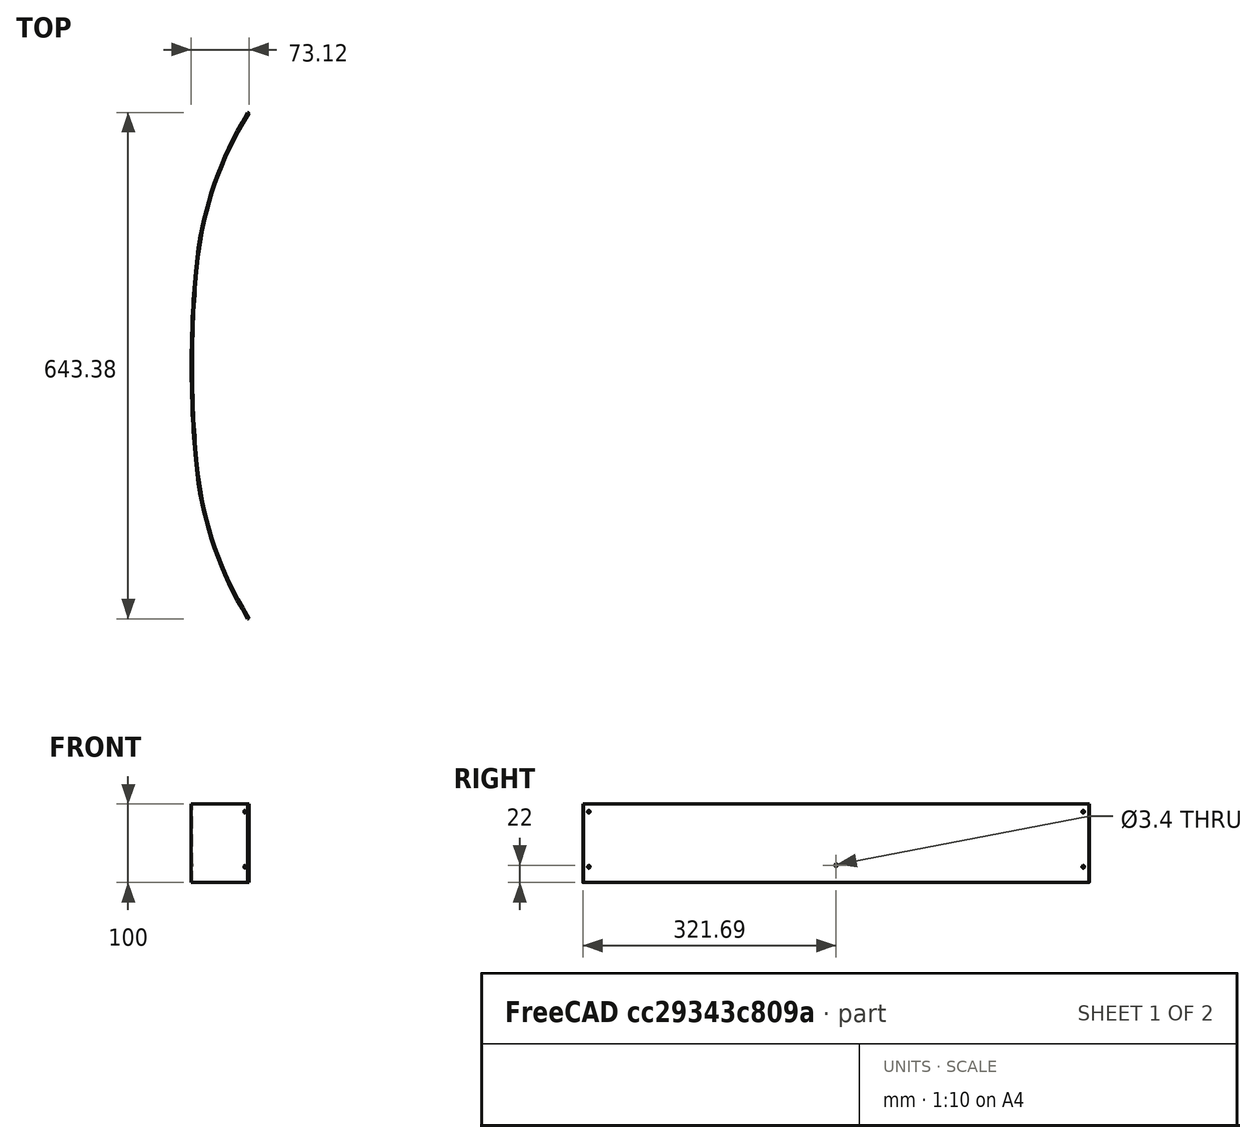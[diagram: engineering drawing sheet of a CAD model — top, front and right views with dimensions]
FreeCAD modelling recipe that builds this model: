
FCSTD DOCUMENT  (FreeCAD 1.1R38827 (Git))
Label: composit_stand3_hat_plexiglass_main
License: All rights reserved
LicenseURL: http://en.wikipedia.org/wiki/All_rights_reserved
objects: Part::Feature×1, PartDesign::SubShapeBinder×1, Part::Mirroring×1, Sketcher::SketchObject×1
note: 5 computed .brp shape members not serialized (recipe doc carries the construction recipe); baked Part::Feature solids carry a one-line shape summary decoded from their .brp
EXTERNAL_REF file=composit_stand3_hat_bottom_main.FCStd obj=Sketch001

FEATURE [Part::Feature] Body172  label="hat3_plexiglass001"
  Placement = pos=(0,0,0) rot=(0,0,1;-0.523599rad)
  shape: bbox 73.12 x 643.4 x 100 mm, 43 faces (baked)
FEATURE [PartDesign::SubShapeBinder] Binder
  BindCopyOnChange = 0
  BindMode = 0
  ClaimChildren = false
  Fuse = false
  MakeFace = true
  OffsetFill = false
  OffsetIntersection = false
  OffsetJoinType = 0
  OffsetOpenResult = false
  PartialLoad = false
  Placement = pos=(0,0,0) rot=(0,0,1;-1.0472rad)
  Relative = true
  Support = -> [<external composit_stand3_hat_bottom_main.FCStd>#Sketch001]
  _Version = 2
FEATURE [Part::Mirroring] Part__Mirroring  label="Binder (Mirror #1)"
  Base = (0,0,0)
  Normal = (0,1,0)
  Source = -> Binder
FEATURE [Sketcher::SketchObject] Sketch  label="main_sketch"
  ArcFitTolerance = 1e-06
  ExternalGeometry = -> [Body172,Part__Mirroring]
  FullyConstrained = true
  MakeInternals = false
  sketch-geometry (4):
    g0: LineSegment StartX=204.116 StartY=320.94 StartZ=0 EndX=116.713 EndY=169.553 EndZ=0
    g1: LineSegment StartX=116.713 StartY=169.553 StartZ=0 EndX=116.713 EndY=-169.553 EndZ=0
    g2: LineSegment StartX=116.713 StartY=-169.553 StartZ=0 EndX=204.116 EndY=-320.94 EndZ=0
    g3: ArcOfCircle [constr] CenterX=713.119 CenterY=9.74631 CenterZ=0 NormalX=0 NormalY=0 NormalZ=1 AngleXU=0 Radius=596.406 StartAngle=2.61799 EndAngle=3.14159
  constraints (11):
    c: Coincident(g0,g1)
    c: Coincident(g2,g1)
    c: Symmetric(g2,g0,g-1)
    c: Symmetric(g1,g0,g-1)
    c: Coincident(g0,g-3)
    c: Angle(g0) = -2.0944
    c: Coincident(g3,g-3)
    c: Tangent(g3,g0)
    c: Tangent(g3,g1) = -1.5708
    c: Radius(g3) = 596.406  'r'
    c: DistanceX(g-5,g3) = 1.5
